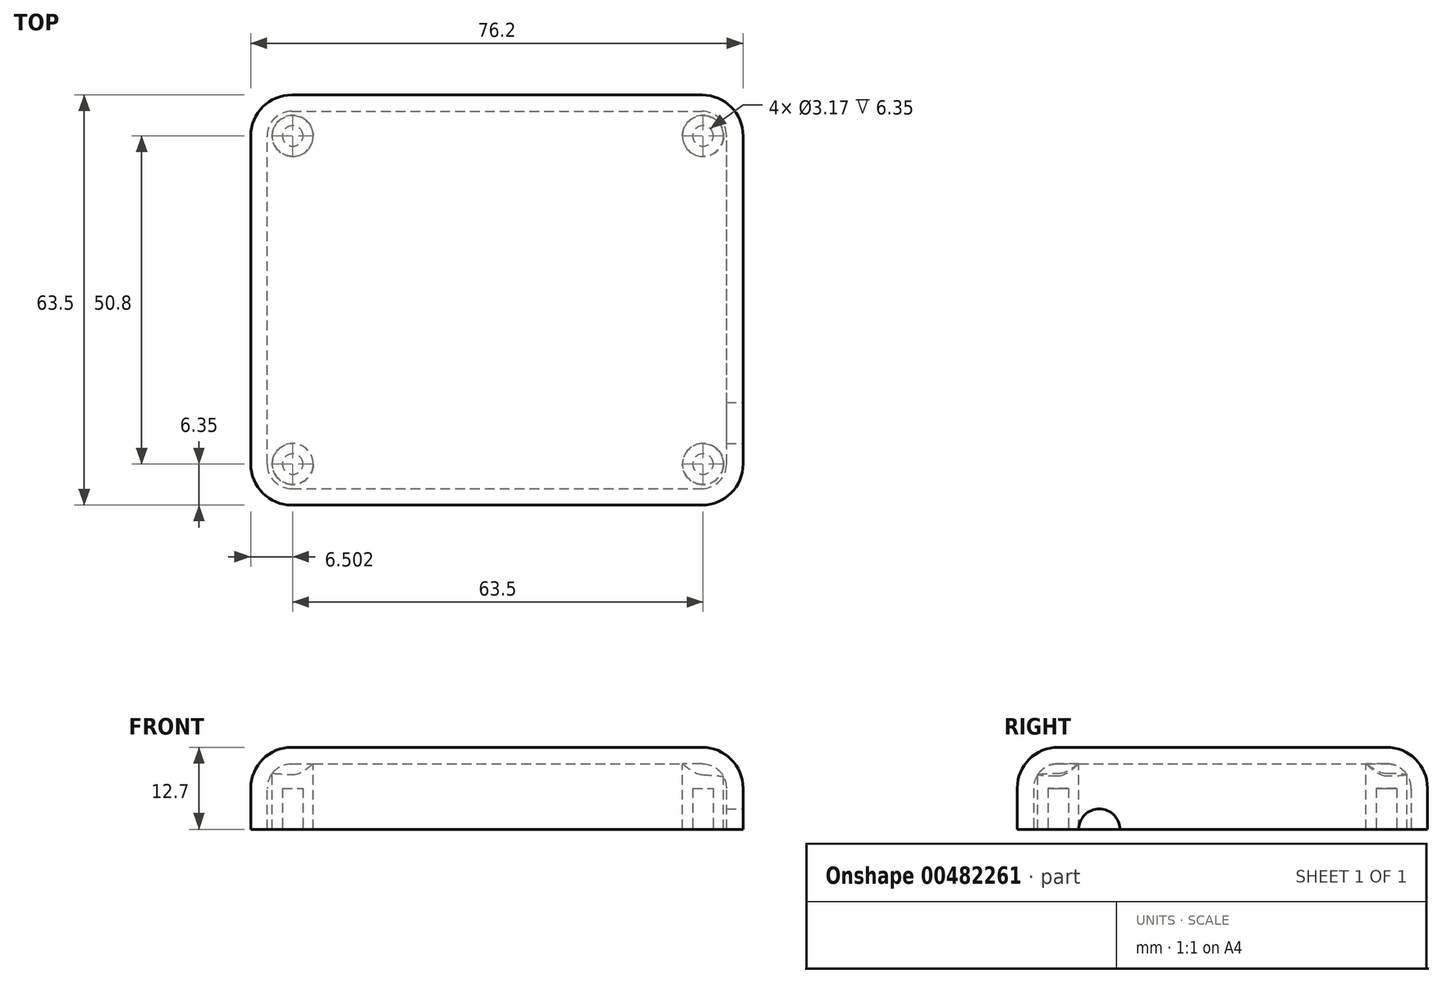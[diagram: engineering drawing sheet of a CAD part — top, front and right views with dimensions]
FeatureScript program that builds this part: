
annotation { "Feature Type Name" : "Feature", "Feature Type Description" : "" }
export const myFeature = defineFeature(function(context is Context, id is Id, definition is map)
    precondition{}
    {
        {
            var Q0;
            Q0=qCreatedBy(makeId("Top.planeOp"),FACE);
            var sketch = newSketch(context, id + "F0", { "sketchPlane" : qUnion([Q0])});
            skLineSegment(sketch, "E0.bottom", {"start": v(31.75, -31.75) * mm, "end": v(-31.75, -31.75) * mm});
            skLineSegment(sketch, "E0.top", {"start": v(31.75, 31.75) * mm, "end": v(-31.75, 31.75) * mm});
            skLineSegment(sketch, "E0.left", {"start": v(38.1, -25.4) * mm, "end": v(38.1, 25.4) * mm});
            skLineSegment(sketch, "E0.right", {"start": v(-38.1, -25.4) * mm, "end": v(-38.1, 25.4) * mm});
            skPoint(sketch, "E0.middle", {"position": v(0, 0) * mm});
            skPoint(sketch, "E1.visualSharp", {"position": v(-38.1, 31.75) * mm});
            skArc(sketch, "E1.filletArc", {"start": v(-31.75, 31.75) * mm, "mid": v(-36.24, 29.9) * mm, "end": v(-38.1, 25.4) * mm});
            skPoint(sketch, "E2.visualSharp", {"position": v(38.1, 31.75) * mm});
            skArc(sketch, "E2.filletArc", {"start": v(38.1, 25.4) * mm, "mid": v(36.24, 29.9) * mm, "end": v(31.75, 31.75) * mm});
            skPoint(sketch, "E3.visualSharp", {"position": v(38.1, -31.75) * mm});
            skArc(sketch, "E3.filletArc", {"start": v(31.75, -31.75) * mm, "mid": v(36.24, -29.9) * mm, "end": v(38.1, -25.4) * mm});
            skPoint(sketch, "E4.visualSharp", {"position": v(-38.1, -31.75) * mm});
            skArc(sketch, "E4.filletArc", {"start": v(-38.1, -25.4) * mm, "mid": v(-36.24, -29.9) * mm, "end": v(-31.75, -31.75) * mm});
            skSolve(sketch);
        }
        {
            var Q0;
            Q0=qSketchRegion(id+"F0",true);
            extrude(context, id + "F1", {"entities" : qUnion([Q0]), "depth" : 12.7 * mm});
        }
        {
            var Q0;
            Q0=makeQuery(id+"F1.opExtrude","CAP_FACE",FACE,{"disambiguationData":[OSD([sQuery(id+"F0.wireOp",EDGE,"E0.bottom"),sQuery(id+"F0.wireOp",EDGE,"E0.top"),sQuery(id+"F0.wireOp",EDGE,"E0.left"),sQuery(id+"F0.wireOp",EDGE,"E0.right")])],"isStart":false});
            fillet(context, id + "F2", {"entities" : qUnion([Q0]), "radius" : 6.35 * mm, "tangentPropagation" : true, "allowEdgeOverflow" : false});
        }
        {
            var Q0;
            Q0=makeQuery(id+"F1.opExtrude","CAP_FACE",FACE,{"disambiguationData":[OSD([sQuery(id+"F0.wireOp",EDGE,"E0.bottom"),sQuery(id+"F0.wireOp",EDGE,"E0.top"),sQuery(id+"F0.wireOp",EDGE,"E0.left"),sQuery(id+"F0.wireOp",EDGE,"E0.right"),sQuery(id+"F0.wireOp",EDGE,"E1.filletArc"),sQuery(id+"F0.wireOp",EDGE,"E2.filletArc"),sQuery(id+"F0.wireOp",EDGE,"E3.filletArc"),sQuery(id+"F0.wireOp",EDGE,"E4.filletArc")])],"isStart":true});
            shell(context, id + "F3", {"entities" : qUnion([Q0]), "thickness" : 2.54 * mm});
        }
        {
            var Q0;
            Q0=makeQuery(id+"F1.opExtrude","SWEPT_FACE",FACE,{"disambiguationData":[OSD([sQuery(id+"F0.wireOp",EDGE,"E0.left")])]});
            var sketch = newSketch(context, id + "F4", { "sketchPlane" : qUnion([Q0])});
            skCircle(sketch, "E5", {"center": v(-19.05, 0) * mm, "radius": 3.18 * mm});
            skSolve(sketch);
        }
        {
            var Q0;
            Q0=qSketchRegion(id+"F4",true);
            var Q1;
            {var subQ0=sQuery(id+"F0.wireOp",EDGE,"E0.right");Q1=makeQuery(id+"F3.opShell","OFFSET_FACE",FACE,{"disambiguationData":[OSD([subQ0]),TDD([makeQuery(id+"F1.opExtrude","SWEPT_FACE",FACE,{"disambiguationData":[OSD([subQ0])]})])]});}
            extrude(context, id + "F5", {"entities" : qUnion([Q0]), "operationType" : NewBodyOperationType.REMOVE, "endBound" : BoundingType.UP_TO_SURFACE, "oppositeDirection" : true, "endBoundEntityFace" : qUnion([Q1]), "depth" : 25.4 * mm});
        }
        {
            var Q0;
            Q0=makeQuery(id+"F3.opShell","OFFSET_FACE",FACE,{"disambiguationData":[OSD([sQuery(id+"F0.wireOp",EDGE,"E0.bottom"),sQuery(id+"F0.wireOp",EDGE,"E0.top"),sQuery(id+"F0.wireOp",EDGE,"E0.left"),sQuery(id+"F0.wireOp",EDGE,"E0.right"),sQuery(id+"F0.wireOp",EDGE,"E1.filletArc"),sQuery(id+"F0.wireOp",EDGE,"E2.filletArc"),sQuery(id+"F0.wireOp",EDGE,"E3.filletArc"),sQuery(id+"F0.wireOp",EDGE,"E4.filletArc")])]});
            cPlane(context, id + "F6", {"entities" : qUnion([Q0]), "cplaneType" : CPlaneType.OFFSET, "offset" : 0 * mm, "width" : 152.4 * mm, "height" : 152.4 * mm});
        }
        {
            var Q0;
            Q0=qCreatedBy(id+"F6.planeOp",FACE);
            var sketch = newSketch(context, id + "F7", { "sketchPlane" : qUnion([Q0])});
            skCircle(sketch, "E6", {"center": v(-31.6, 25.4) * mm, "radius": 3.18 * mm});
            skCircle(sketch, "E7.0.1.0", {"center": v(-31.6, -25.4) * mm, "radius": 3.18 * mm});
            skCircle(sketch, "E7.1.0.0", {"center": v(31.9, 25.4) * mm, "radius": 3.18 * mm});
            skCircle(sketch, "E7.1.1.0", {"center": v(31.9, -25.4) * mm, "radius": 3.18 * mm});
            skLineSegment(sketch, "E7.direction1", {"start": v(-31.6, 25.4) * mm, "end": v(31.9, 25.4) * mm, "construction": true});
            skLineSegment(sketch, "E7.direction2", {"start": v(-31.6, 25.4) * mm, "end": v(-31.6, -25.4) * mm, "construction": true});
            skSolve(sketch);
        }
        {
            var Q0;
            Q0=qSketchRegion(id+"F7",true);
            var Q1;
            Q1=makeQuery(id+"F1.opExtrude","CAP_FACE",FACE,{"disambiguationData":[OSD([sQuery(id+"F0.wireOp",EDGE,"E0.bottom"),sQuery(id+"F0.wireOp",EDGE,"E0.top"),sQuery(id+"F0.wireOp",EDGE,"E0.left"),sQuery(id+"F0.wireOp",EDGE,"E0.right"),sQuery(id+"F0.wireOp",EDGE,"E1.filletArc"),sQuery(id+"F0.wireOp",EDGE,"E2.filletArc"),sQuery(id+"F0.wireOp",EDGE,"E3.filletArc"),sQuery(id+"F0.wireOp",EDGE,"E4.filletArc")])],"isStart":true});
            extrude(context, id + "F8", {"entities" : qUnion([Q0]), "operationType" : NewBodyOperationType.ADD, "endBound" : BoundingType.UP_TO_SURFACE, "endBoundEntityFace" : qUnion([Q1]), "depth" : 12.7 * mm});
        }
        {
            var Q0;
            Q0=makeQuery(id+"F8.opExtrude","CAP_FACE",FACE,{"disambiguationData":[OSD([sQuery(id+"F7.wireOp",EDGE,"E6")])],"isStart":false});
            var sketch = newSketch(context, id + "F9", { "sketchPlane" : qUnion([Q0])});
            skCircle(sketch, "E8", {"center": v(-31.6, 25.4) * mm, "radius": 1.59 * mm});
            skCircle(sketch, "E9.0.1.0", {"center": v(-31.6, -25.4) * mm, "radius": 1.59 * mm});
            skCircle(sketch, "E9.1.0.0", {"center": v(31.9, 25.4) * mm, "radius": 1.59 * mm});
            skCircle(sketch, "E9.1.1.0", {"center": v(31.9, -25.4) * mm, "radius": 1.59 * mm});
            skLineSegment(sketch, "E9.direction1", {"start": v(-31.6, 25.4) * mm, "end": v(31.9, 25.4) * mm, "construction": true});
            skLineSegment(sketch, "E9.direction2", {"start": v(-31.6, 25.4) * mm, "end": v(-31.6, -25.4) * mm, "construction": true});
            skSolve(sketch);
        }
        {
            var Q0;
            Q0 = qSketchRegion(id + "F9", true);
            extrude(context, id + "F10", {"entities" : qUnion([Q0]), "operationType" : NewBodyOperationType.REMOVE, "oppositeDirection" : true, "depth" : 6.35 * mm});
        }
    });
